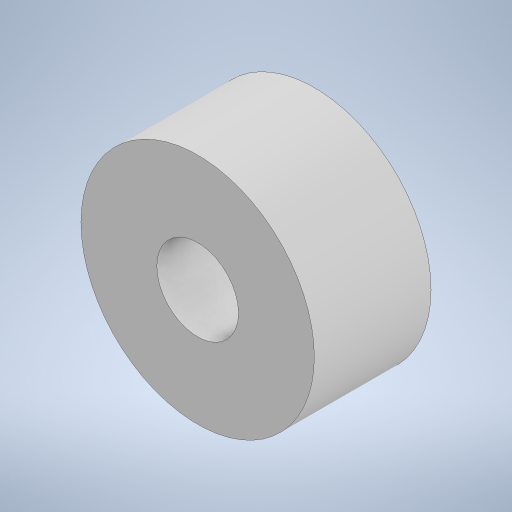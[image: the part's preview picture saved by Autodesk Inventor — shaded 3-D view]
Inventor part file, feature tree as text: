
AUTODESK INVENTOR PART (.ipt)
format: ipt  version: 2024 (Build 280153000, 153)  size: 205,824 bytes
history: native  units: mm
features: other x1, extrude x1, sketch x1
ambient origin geometry x8: Origin, YZ Plane, XZ Plane, XY Plane, X Axis, Y Axis, Z Axis, Center Point
bodies: Body1 (feature_tree)
feature tree (3):
  other  "ソリッド1"
  extrude  "押し出し1"  Depth=3.5mm
  sketch  "スケッチ1"
